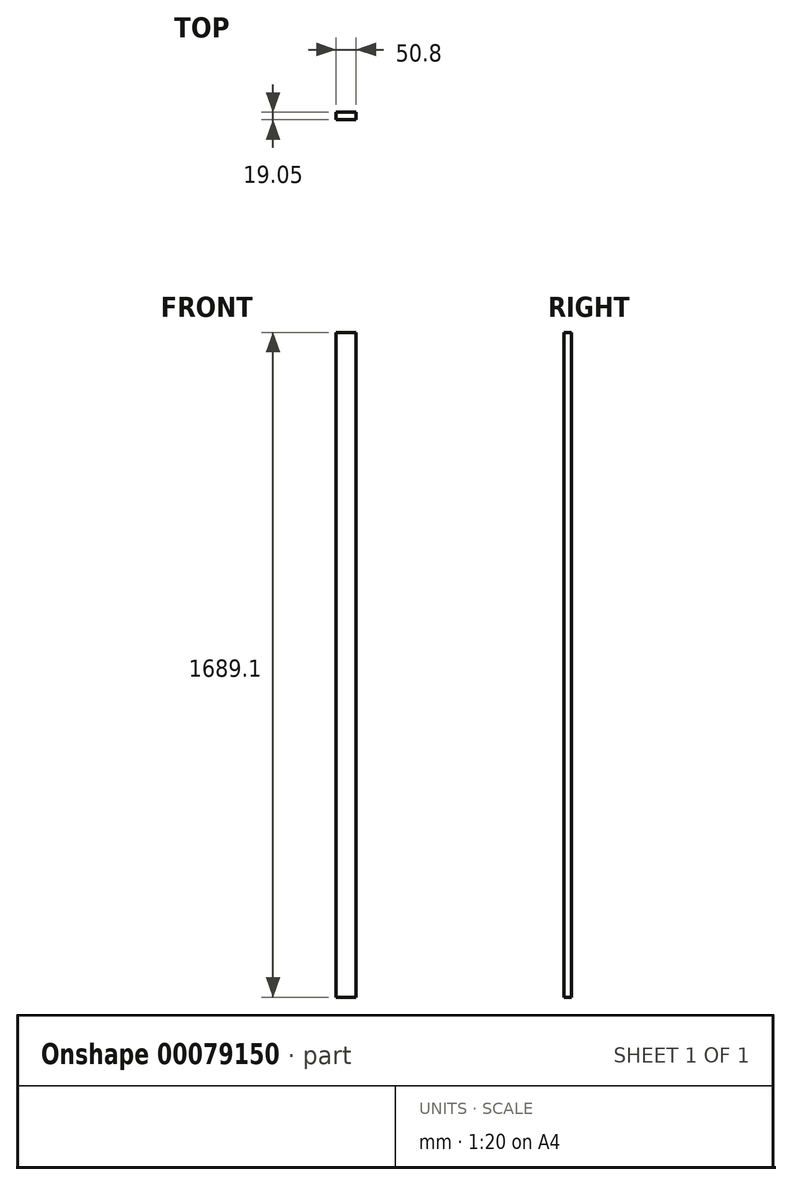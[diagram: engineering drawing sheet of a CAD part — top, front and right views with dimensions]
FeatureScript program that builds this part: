
annotation { "Feature Type Name" : "Feature", "Feature Type Description" : "" }
export const myFeature = defineFeature(function(context is Context, id is Id, definition is map)
    precondition{}
    {
        {
            var Q0;
            Q0=qCreatedBy(makeId("Front.planeOp"),FACE);
            var sketch = newSketch(context, id + "F0", { "sketchPlane" : qUnion([Q0])});
            skLineSegment(sketch, "E0.bottom", {"start": v(-70.25, 1630.13) * mm, "end": v(-19.45, 1630.13) * mm});
            skLineSegment(sketch, "E0.top", {"start": v(-70.25, -58.97) * mm, "end": v(-19.45, -58.97) * mm});
            skLineSegment(sketch, "E0.left", {"start": v(-70.25, 1630.13) * mm, "end": v(-70.25, -58.97) * mm});
            skLineSegment(sketch, "E0.right", {"start": v(-19.45, 1630.13) * mm, "end": v(-19.45, -58.97) * mm});
            skSolve(sketch);
        }
        {
            var Q0;
            Q0=makeQuery(id+"F0.imprint","IMPRINT",FACE,{"disambiguationData":[TD([[makeQuery(id+"F0.imprint","IMPRINT",EDGE,{"derivedFrom":sQuery(id+"F0.wireOp",EDGE,"E0.bottom")}),-1.0]])]});
            extrude(context, id + "F1", {"entities" : qUnion([Q0]), "depth" : 19.05 * mm});
        }
    });
